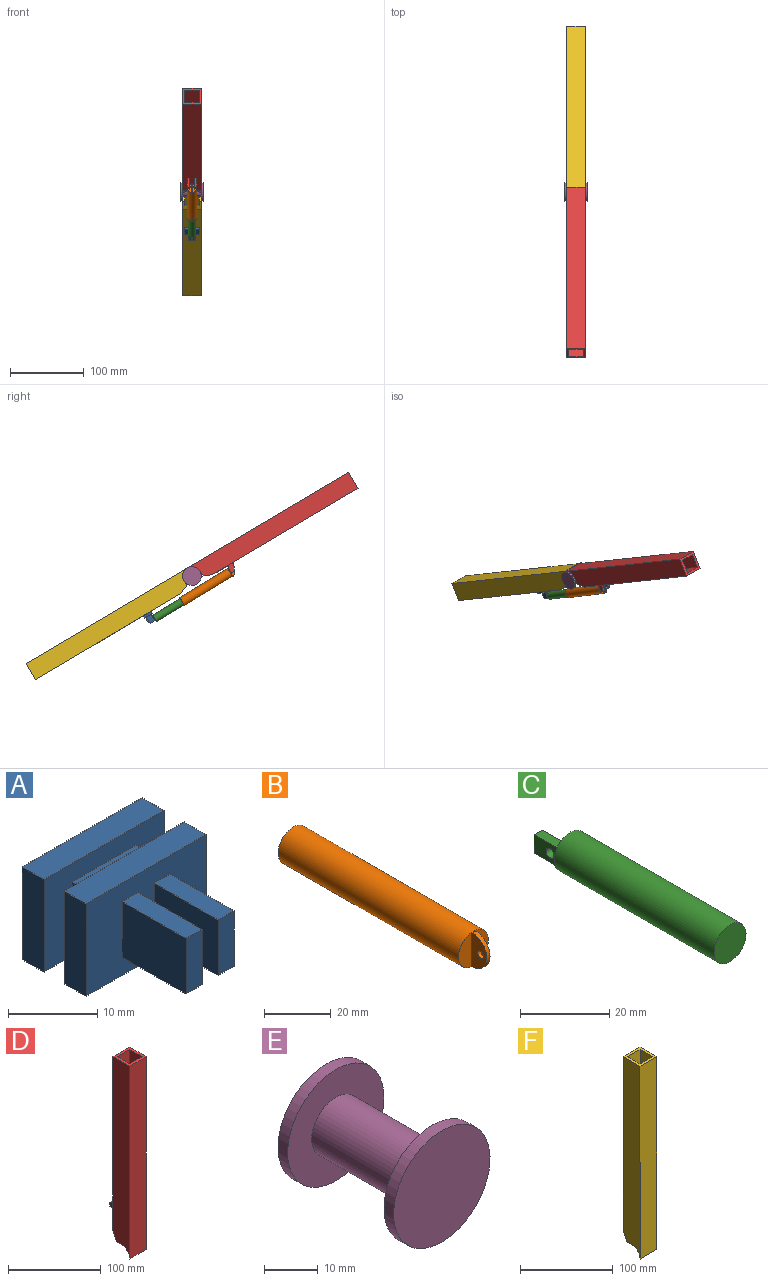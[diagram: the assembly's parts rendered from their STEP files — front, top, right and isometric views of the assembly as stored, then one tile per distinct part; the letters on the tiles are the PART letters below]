
ASSEMBLY  parts=6 mates=7
PART A: 27 faces, bbox 19.1x20.3x12.7 mm
  f0: plane 19.05x12.7mm, normal (0,-1,0), area 203.2mm2, adj f12,f13,f14,f15,f16,f17,f18,f19
  f1: plane 12.7x3.49mm, normal (1,0,0), area 44.4mm2, adj f2,f4,f5,f11
  f2: plane 19.05x3.49mm, normal (0,0,1), area 66.5mm2, adj f1,f3,f5,f11
  f3: plane 12.7x3.49mm, normal (-1,0,0), area 44.4mm2, adj f2,f4,f5,f11
  f4: plane 19.05x3.49mm, normal (0,0,-1), area 66.5mm2, adj f1,f3,f5,f11
  f5: plane 19.05x12.7mm, normal (0,1,0), area 241.9mm2, adj f1,f2,f3,f4
  f6: plane 7.62x3.18mm, normal (-1,0,0), area 24.2mm2, adj f7,f9,f10,f11
  f7: plane 10.16x3.18mm, normal (0,0,1), area 32.3mm2, adj f6,f8,f10,f11
  f8: plane 7.62x3.18mm, normal (1,0,0), area 24.2mm2, adj f7,f9,f10,f11
  f9: plane 10.16x3.18mm, normal (0,0,-1), area 32.3mm2, adj f6,f8,f10,f11
  f10: plane 19.05x12.7mm, normal (0,1,0), area 164.5mm2, adj f6,f7,f8,f9,f12,f13,f14,f15
  f11: plane 19.05x12.7mm, normal (0,-1,0), area 164.5mm2, adj f1,f2,f3,f4,f6,f7,f8,f9
  f12: plane 19.05x3.49mm, normal (0,0,-1), area 66.5mm2, adj f0,f10,f13,f15
  f13: plane 12.7x3.49mm, normal (-1,0,0), area 44.4mm2, adj f0,f10,f12,f14
  f14: plane 19.05x3.49mm, normal (0,0,1), area 66.5mm2, adj f0,f10,f13,f15
  f15: plane 12.7x3.49mm, normal (1,0,0), area 44.4mm2, adj f0,f10,f12,f14
  f16: plane 10.16x2.54mm, normal (0,0,1), area 25.8mm2, adj f0,f17,f19,f20
  f17: plane 10.16x7.62mm, normal (-1,0,0), area 72.4mm2, adj f0,f16,f18,f20,f26
  f18: plane 10.16x2.54mm, normal (0,0,-1), area 25.8mm2, adj f0,f17,f19,f20
  f19: plane 10.16x7.62mm, normal (1,0,0), area 77.4mm2, adj f0,f16,f18,f20
  f20: plane 7.62x2.54mm, normal (0,-1,0), area 19.4mm2, adj f16,f17,f18,f19
  f21: plane 10.16x7.62mm, normal (1,0,0), area 72.4mm2, adj f0,f22,f24,f25,f26
  f22: plane 10.16x2.54mm, normal (0,0,1), area 25.8mm2, adj f0,f21,f23,f25
  f23: plane 10.16x7.62mm, normal (-1,0,0), area 77.4mm2, adj f0,f22,f24,f25
  f24: plane 10.16x2.54mm, normal (0,0,-1), area 25.8mm2, adj f0,f21,f23,f25
  f25: plane 7.62x2.54mm, normal (0,-1,0), area 19.4mm2, adj f21,f22,f23,f24
  f26: cylinder r=1.27mm len=2.54mm, axis (1,0,0), area 20.3mm2, adj f17,f21
PART B: 10 faces, bbox 12.7x82.6x12.7 mm
  f0: cylinder r=6.35mm len=76.89mm, axis (0,1,0), area 3041.2mm2, adj f1,f2,f4,f5,f7,f8
  f1: plane 12.63x6.35mm, normal (1,0,0), area 58.2mm2, adj f0,f2,f8,f9
  f2: plane 12.63x5.66mm, normal (0,-1,0), area 54.6mm2, adj f0,f1
  f3: cylinder r=5.08mm len=73.66mm, axis (0,1,0), area 2351.1mm2, adj f5,f6
  f4: plane 12.63x5.66mm, normal (0,-1,0), area 54.6mm2, adj f0,f7
  f5: plane 12.7x12.7mm, normal (0,1,0), area 45.6mm2, adj f0,f3
  f6: plane 10.16x10.16mm, normal (0,1,0), area 81.1mm2, adj f3
  f7: plane 12.63x6.35mm, normal (-1,0,0), area 58.2mm2, adj f0,f4,f8,f9
  f8: cylinder r=6.35mm len=12.7mm, axis (-1,0,0), area 26.6mm2, adj f0,f1,f7
  f9: cylinder r=1.27mm len=2.54mm, axis (-1,0,0), area 11mm2, adj f1,f7
PART C: 11 faces, bbox 10.2x61x10.2 mm
  f0: cylinder r=5.08mm len=50.8mm, axis (0,-1,0), area 1621.5mm2, adj f1,f2,f4,f10
  f1: plane 10.16x10mm, normal (0,1,0), area 68.3mm2, adj f0,f3,f8,f9
  f2: plane 1.27x0.16mm, normal (0,-1,0), area 0.1mm2, adj f0,f5,f8
  f3: plane 10.16x2.54mm, normal (0,0,1), area 25.8mm2, adj f1,f7,f8,f9
  f4: plane 1.27x0.16mm, normal (0,-1,0), area 0.1mm2, adj f0,f5,f9
  f5: plane 10.16x2.54mm, normal (0,0,-1), area 25.8mm2, adj f2,f4,f7,f8,f9
  f6: cylinder r=1.27mm len=2.54mm, axis (-1,0,0), area 20.3mm2, adj f8,f9
  f7: plane 5.08x2.54mm, normal (0,1,0), area 12.9mm2, adj f3,f5,f8,f9
  f8: plane 10.16x5.08mm, normal (1,0,0), area 46.5mm2, adj f1,f2,f3,f5,f6,f7
  f9: plane 10.16x5.08mm, normal (-1,0,0), area 46.5mm2, adj f1,f3,f4,f5,f6,f7
  f10: plane 10.16x10.16mm, normal (0,-1,0), area 81.1mm2, adj f0
PART D: 24 faces, bbox 25.4x36.8x254 mm
  f0: plane 254x25.4mm, normal (-1,0,0), area 6131.4mm2, adj f2,f3,f4,f10,f11,f12
  f1: plane 254x25.4mm, normal (1,0,0), area 6131.4mm2, adj f2,f3,f4,f9,f10,f11
  f2: plane 228.6x25.4mm, normal (0,1,0), area 5759.5mm2, adj f0,f1,f3,f11,f13,f14,f15,f16
  f3: plane 25.4x25.4mm, normal (0,0,1), area 282.3mm2, adj f0,f1,f2,f4,f5,f6,f7,f8
  f4: plane 254x25.4mm, normal (0,-1,0), area 6451.6mm2, adj f0,f1,f3,f10
  f5: plane 245.6x19.05mm, normal (1,0,0), area 4604.8mm2, adj f3,f6,f8,f10,f11,f12
  f6: plane 236.54x19.05mm, normal (0,-1,0), area 4506mm2, adj f3,f5,f7,f11
  f7: plane 245.6x19.05mm, normal (-1,0,0), area 4604.8mm2, adj f3,f6,f8,f9,f10,f11
  f8: plane 245.6x19.05mm, normal (0,1,0), area 4678.7mm2, adj f3,f5,f7,f10
  f9: plane 7.62x3.18mm, normal (0,0,-1), area 24.2mm2, adj f1,f7,f10,f11
  f10: cylinder r=12.7mm len=25.4mm, axis (1,0,0), area 301.5mm2, adj f0,f1,f4,f5,f7,f8,f9,f12
  f11: plane 25.4x12.7mm, normal (0,0.93,-0.37), area 249.7mm2, adj f0,f1,f2,f5,f6,f7,f9,f12
  f12: plane 7.62x3.18mm, normal (0,0,-1), area 24.2mm2, adj f0,f5,f10,f11
  f13: plane 11.43x9.24mm, normal (-1,0,0), area 76.8mm2, adj f2,f14,f16,f17,f23
  f14: plane 11.43x4.16mm, normal (0,0.34,0.94), area 30.9mm2, adj f2,f13,f15,f17
  f15: plane 11.43x9.24mm, normal (1,0,0), area 81.8mm2, adj f2,f14,f16,f17
  f16: plane 11.43x2.54mm, normal (0,0,-1), area 29mm2, adj f2,f13,f15,f17
  f17: plane 5.08x2.54mm, normal (0,1,0), area 12.9mm2, adj f13,f14,f15,f16
  f18: plane 11.43x9.24mm, normal (-1,0,0), area 81.8mm2, adj f2,f19,f21,f22
  f19: plane 11.43x4.16mm, normal (0,0.34,0.94), area 30.9mm2, adj f2,f18,f20,f22
  f20: plane 11.43x9.24mm, normal (1,0,0), area 76.8mm2, adj f2,f19,f21,f22,f23
  f21: plane 11.43x2.54mm, normal (0,0,-1), area 29mm2, adj f2,f18,f20,f22
  f22: plane 5.08x2.54mm, normal (0,1,0), area 12.9mm2, adj f18,f19,f20,f21
  f23: cylinder r=1.27mm len=7.62mm, axis (1,0,0), area 60.8mm2, adj f13,f20
PART E: 7 faces, bbox 25.4x30.5x25.4 mm
  f0: cylinder r=12.7mm len=25.4mm, axis (0,1,0), area 202.7mm2, adj f1,f3
  f1: plane 25.4x25.4mm, normal (0,-1,0), area 506.7mm2, adj f0
  f2: cylinder r=6.35mm len=25.4mm, axis (0,1,0), area 1013.4mm2, adj f3,f4
  f3: plane 25.4x25.4mm, normal (0,1,0), area 380mm2, adj f0,f2
  f4: plane 25.4x25.4mm, normal (0,-1,0), area 380mm2, adj f2,f6
  f5: plane 25.4x25.4mm, normal (0,1,0), area 506.7mm2, adj f6
  f6: cylinder r=12.7mm len=25.4mm, axis (0,1,0), area 202.7mm2, adj f4,f5
PART F: 17 faces, bbox 25.4x25.4x254 mm
  f0: plane 228.6x25.4mm, normal (0,1,0), area 5290.3mm2, adj f2,f3,f4,f11,f13,f14,f15,f16
  f1: plane 236.54x19.05mm, normal (0,-1,0), area 3989.9mm2, adj f4,f6,f7,f11,f13,f14,f15,f16
  f2: plane 254x25.4mm, normal (-1,0,0), area 6131.4mm2, adj f0,f4,f5,f10,f11,f12
  f3: plane 254x25.4mm, normal (1,0,0), area 6131.4mm2, adj f0,f4,f5,f9,f10,f11
  f4: plane 25.4x25.4mm, normal (0,0,1), area 282.3mm2, adj f0,f1,f2,f3,f5,f6,f7,f8
  f5: plane 254x25.4mm, normal (0,-1,0), area 6451.6mm2, adj f2,f3,f4,f10
  f6: plane 245.6x19.05mm, normal (1,0,0), area 4604.8mm2, adj f1,f4,f8,f10,f11,f12
  f7: plane 245.6x19.05mm, normal (-1,0,0), area 4604.8mm2, adj f1,f4,f8,f9,f10,f11
  f8: plane 245.6x19.05mm, normal (0,1,0), area 4678.7mm2, adj f4,f6,f7,f10
  f9: plane 7.62x3.18mm, normal (0,0,-1), area 24.2mm2, adj f3,f7,f10,f11
  f10: cylinder r=12.7mm len=25.4mm, axis (1,0,0), area 301.5mm2, adj f2,f3,f5,f6,f7,f8,f9,f12
  f11: plane 25.4x12.7mm, normal (0,0.93,-0.37), area 249.7mm2, adj f0,f1,f2,f3,f6,f7,f9,f12
  f12: plane 7.62x3.18mm, normal (0,0,-1), area 24.2mm2, adj f2,f6,f10,f11
  f13: plane 50.8x3.18mm, normal (-1,0,0), area 161.3mm2, adj f0,f1,f14,f16
  f14: plane 10.16x3.18mm, normal (0,0,1), area 32.3mm2, adj f0,f1,f13,f15
  f15: plane 50.8x3.18mm, normal (1,0,0), area 161.3mm2, adj f0,f1,f14,f16
  f16: plane 10.16x3.18mm, normal (0,0,-1), area 32.3mm2, adj f0,f1,f13,f15
PLACE A rot(axis=(1,0,0),59.3deg) t=(-109.26,41.93,-80.08)mm
PLACE B rot(axis=(0,0.96,-0.27),180deg) t=(-109.26,-6.2,-65.61)mm
PLACE C rot(axis=(0,0.96,-0.27),180deg) t=(-109.26,-33.98,-48.67)mm
PLACE D rot(axis=(0,-0.49,0.87),180deg) t=(-96.56,-25.96,-41.67)mm
PLACE E rot(axis=(-0.66,-0.66,-0.37),139.4deg) t=(-109.26,-19.48,-30.75)mm
PLACE F rot(axis=(-1,0,0),120.7deg) t=(-121.96,-25.96,-41.67)mm fixed
MATE revolute D.f10 <-> F.f10  axis (-1,0,0) through (-121.96,-19.48,-30.75)mm
MATE revolute B.f9 <-> D.f23  axis (1,0,0) through (-109.26,-74.51,-23.95)mm
MATE revolute E.f2 <-> D.f10  axis (1,0,0) through (-121.96,-19.48,-30.75)mm
MATE planar A.f10 <-> F.f0  axis (0,0.51,0.86) through (-109.26,41.12,-81.44)mm
MATE revolute C.f6 <-> A.f26  axis (1,0,0) through (-109.26,36.74,-88.82)mm
MATE planar A.f6 <-> F.f15  axis (-1,0,0) through (-114.34,41.93,-80.08)mm
MATE slider C.f0 <-> B.f3  axis (0,-0.85,0.52) through (-109.26,-12.29,-61.89)mm
